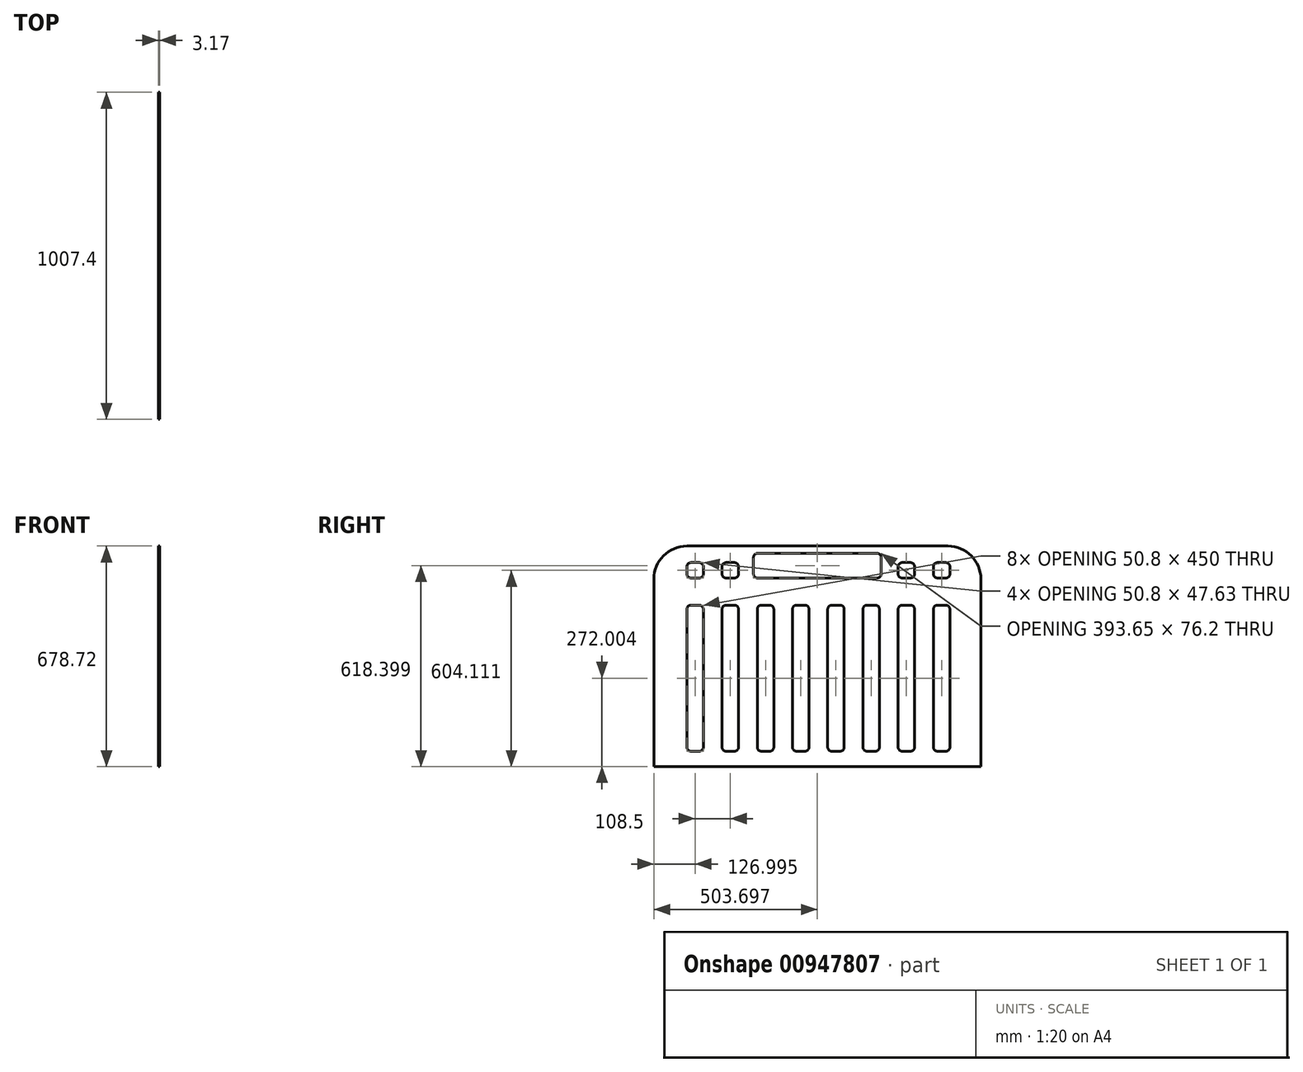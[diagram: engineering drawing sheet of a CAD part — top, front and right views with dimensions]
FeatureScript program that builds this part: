
annotation { "Feature Type Name" : "Feature", "Feature Type Description" : "" }
export const myFeature = defineFeature(function(context is Context, id is Id, definition is map)
    precondition{}
    {
        {
            var Q0;
            Q0=qCreatedBy(makeId("Right.planeOp"),FACE);
            var sketch = newSketch(context, id + "F0", { "sketchPlane" : qUnion([Q0])});
            skLineSegment(sketch, "E0", {"start": v(-521.4, 162.17) * mm, "end": v(-521.4, -414.95) * mm});
            skLineSegment(sketch, "E1", {"start": v(-521.4, -414.95) * mm, "end": v(486, -414.95) * mm});
            skLineSegment(sketch, "E2", {"start": v(486, -414.95) * mm, "end": v(486, 162.17) * mm});
            skLineSegment(sketch, "E3", {"start": v(-419.8, 263.77) * mm, "end": v(384.4, 263.77) * mm});
            skArc(sketch, "E4", {"start": v(486, 162.17) * mm, "mid": v(456.24, 234.02) * mm, "end": v(384.4, 263.77) * mm});
            skArc(sketch, "E5", {"start": v(-419.8, 263.77) * mm, "mid": v(-491.65, 234.02) * mm, "end": v(-521.4, 162.17) * mm});
            skLineSegment(sketch, "E6.bottom", {"start": v(-407.1, 82.05) * mm, "end": v(-381.7, 82.05) * mm});
            skLineSegment(sketch, "E6.top", {"start": v(-407.1, -367.95) * mm, "end": v(-381.7, -367.95) * mm});
            skLineSegment(sketch, "E6.left", {"start": v(-419.8, 69.35) * mm, "end": v(-419.8, -355.25) * mm});
            skLineSegment(sketch, "E6.right", {"start": v(-369, 69.35) * mm, "end": v(-369, -355.25) * mm});
            skPoint(sketch, "E7.visualSharp", {"position": v(-419.8, 82.05) * mm});
            skArc(sketch, "E7.filletArc", {"start": v(-407.1, 82.05) * mm, "mid": v(-416.08, 78.33) * mm, "end": v(-419.8, 69.35) * mm});
            skPoint(sketch, "E8.visualSharp", {"position": v(-369, 82.05) * mm});
            skArc(sketch, "E8.filletArc", {"start": v(-369, 69.35) * mm, "mid": v(-372.72, 78.33) * mm, "end": v(-381.7, 82.05) * mm});
            skPoint(sketch, "E9.visualSharp", {"position": v(-369, -367.95) * mm});
            skArc(sketch, "E9.filletArc", {"start": v(-381.7, -367.95) * mm, "mid": v(-372.72, -364.23) * mm, "end": v(-369, -355.25) * mm});
            skPoint(sketch, "E10.visualSharp", {"position": v(-419.8, -367.95) * mm});
            skArc(sketch, "E10.filletArc", {"start": v(-419.8, -355.25) * mm, "mid": v(-416.08, -364.23) * mm, "end": v(-407.1, -367.95) * mm});
            skPoint(sketch, "E11.1.0.0", {"position": v(-311.3, -367.95) * mm});
            skPoint(sketch, "E11.1.0.1", {"position": v(-260.5, -367.95) * mm});
            skPoint(sketch, "E11.1.0.2", {"position": v(-311.3, 114.55) * mm});
            skLineSegment(sketch, "E11.1.0.3", {"start": v(-311.3, 69.35) * mm, "end": v(-311.3, -355.25) * mm});
            skPoint(sketch, "E11.1.0.4", {"position": v(-260.5, 82.05) * mm});
            skLineSegment(sketch, "E11.1.0.5", {"start": v(-260.5, 69.35) * mm, "end": v(-260.5, -355.25) * mm});
            skArc(sketch, "E11.1.0.6", {"start": v(-260.5, 69.35) * mm, "mid": v(-264.22, 78.33) * mm, "end": v(-273.2, 82.05) * mm});
            skLineSegment(sketch, "E11.1.0.7", {"start": v(-298.6, -367.95) * mm, "end": v(-273.2, -367.95) * mm});
            skLineSegment(sketch, "E11.1.0.8", {"start": v(-298.6, 82.05) * mm, "end": v(-273.2, 82.05) * mm});
            skArc(sketch, "E11.1.0.9", {"start": v(-311.3, -355.25) * mm, "mid": v(-307.58, -364.23) * mm, "end": v(-298.6, -367.95) * mm});
            skArc(sketch, "E11.1.0.10", {"start": v(-298.6, 82.05) * mm, "mid": v(-307.58, 78.33) * mm, "end": v(-311.3, 69.35) * mm});
            skArc(sketch, "E11.1.0.11", {"start": v(-273.2, -367.95) * mm, "mid": v(-264.22, -364.23) * mm, "end": v(-260.5, -355.25) * mm});
            skPoint(sketch, "E11.2.0.0", {"position": v(-202.8, -367.95) * mm});
            skPoint(sketch, "E11.2.0.1", {"position": v(-152, -367.95) * mm});
            skPoint(sketch, "E11.2.0.2", {"position": v(-202.8, 114.55) * mm});
            skLineSegment(sketch, "E11.2.0.3", {"start": v(-202.8, 69.35) * mm, "end": v(-202.8, -355.25) * mm});
            skPoint(sketch, "E11.2.0.4", {"position": v(-152, 114.55) * mm});
            skLineSegment(sketch, "E11.2.0.5", {"start": v(-152, 69.35) * mm, "end": v(-152, -355.25) * mm});
            skArc(sketch, "E11.2.0.6", {"start": v(-152, 69.35) * mm, "mid": v(-155.72, 78.33) * mm, "end": v(-164.7, 82.05) * mm});
            skLineSegment(sketch, "E11.2.0.7", {"start": v(-190.1, -367.95) * mm, "end": v(-164.7, -367.95) * mm});
            skLineSegment(sketch, "E11.2.0.8", {"start": v(-190.1, 82.05) * mm, "end": v(-164.7, 82.05) * mm});
            skArc(sketch, "E11.2.0.9", {"start": v(-202.8, -355.25) * mm, "mid": v(-199.08, -364.23) * mm, "end": v(-190.1, -367.95) * mm});
            skArc(sketch, "E11.2.0.10", {"start": v(-190.1, 82.05) * mm, "mid": v(-199.08, 78.33) * mm, "end": v(-202.8, 69.35) * mm});
            skArc(sketch, "E11.2.0.11", {"start": v(-164.7, -367.95) * mm, "mid": v(-155.72, -364.23) * mm, "end": v(-152, -355.25) * mm});
            skPoint(sketch, "E11.3.0.0", {"position": v(-94.3, -367.95) * mm});
            skPoint(sketch, "E11.3.0.1", {"position": v(-43.5, -367.95) * mm});
            skPoint(sketch, "E11.3.0.2", {"position": v(-94.3, 114.55) * mm});
            skLineSegment(sketch, "E11.3.0.3", {"start": v(-94.3, 69.35) * mm, "end": v(-94.3, -355.25) * mm});
            skPoint(sketch, "E11.3.0.4", {"position": v(-43.5, 114.55) * mm});
            skLineSegment(sketch, "E11.3.0.5", {"start": v(-43.5, 69.35) * mm, "end": v(-43.5, -355.25) * mm});
            skArc(sketch, "E11.3.0.6", {"start": v(-43.5, 69.35) * mm, "mid": v(-47.22, 78.33) * mm, "end": v(-56.2, 82.05) * mm});
            skLineSegment(sketch, "E11.3.0.7", {"start": v(-81.6, -367.95) * mm, "end": v(-56.2, -367.95) * mm});
            skLineSegment(sketch, "E11.3.0.8", {"start": v(-81.6, 82.05) * mm, "end": v(-56.2, 82.05) * mm});
            skArc(sketch, "E11.3.0.9", {"start": v(-94.3, -355.25) * mm, "mid": v(-90.58, -364.23) * mm, "end": v(-81.6, -367.95) * mm});
            skArc(sketch, "E11.3.0.10", {"start": v(-81.6, 82.05) * mm, "mid": v(-90.58, 78.33) * mm, "end": v(-94.3, 69.35) * mm});
            skArc(sketch, "E11.3.0.11", {"start": v(-56.2, -367.95) * mm, "mid": v(-47.22, -364.23) * mm, "end": v(-43.5, -355.25) * mm});
            skPoint(sketch, "E11.4.0.0", {"position": v(14.2, -367.95) * mm});
            skPoint(sketch, "E11.4.0.1", {"position": v(65, -367.95) * mm});
            skPoint(sketch, "E11.4.0.2", {"position": v(14.2, 114.55) * mm});
            skLineSegment(sketch, "E11.4.0.3", {"start": v(14.2, 69.35) * mm, "end": v(14.2, -355.25) * mm});
            skPoint(sketch, "E11.4.0.4", {"position": v(65, 114.55) * mm});
            skLineSegment(sketch, "E11.4.0.5", {"start": v(65, 69.35) * mm, "end": v(65, -355.25) * mm});
            skArc(sketch, "E11.4.0.6", {"start": v(65, 69.35) * mm, "mid": v(61.28, 78.33) * mm, "end": v(52.3, 82.05) * mm});
            skLineSegment(sketch, "E11.4.0.7", {"start": v(26.9, -367.95) * mm, "end": v(52.3, -367.95) * mm});
            skLineSegment(sketch, "E11.4.0.8", {"start": v(26.9, 82.05) * mm, "end": v(52.3, 82.05) * mm});
            skArc(sketch, "E11.4.0.9", {"start": v(14.2, -355.25) * mm, "mid": v(17.92, -364.23) * mm, "end": v(26.9, -367.95) * mm});
            skArc(sketch, "E11.4.0.10", {"start": v(26.9, 82.05) * mm, "mid": v(17.92, 78.33) * mm, "end": v(14.2, 69.35) * mm});
            skArc(sketch, "E11.4.0.11", {"start": v(52.3, -367.95) * mm, "mid": v(61.28, -364.23) * mm, "end": v(65, -355.25) * mm});
            skPoint(sketch, "E11.5.0.0", {"position": v(122.7, -367.95) * mm});
            skPoint(sketch, "E11.5.0.1", {"position": v(173.5, -367.95) * mm});
            skPoint(sketch, "E11.5.0.2", {"position": v(122.7, 114.55) * mm});
            skLineSegment(sketch, "E11.5.0.3", {"start": v(122.7, 69.35) * mm, "end": v(122.7, -355.25) * mm});
            skPoint(sketch, "E11.5.0.4", {"position": v(173.5, 114.55) * mm});
            skLineSegment(sketch, "E11.5.0.5", {"start": v(173.5, 69.35) * mm, "end": v(173.5, -355.25) * mm});
            skArc(sketch, "E11.5.0.6", {"start": v(173.5, 69.35) * mm, "mid": v(169.78, 78.33) * mm, "end": v(160.8, 82.05) * mm});
            skLineSegment(sketch, "E11.5.0.7", {"start": v(135.4, -367.95) * mm, "end": v(160.8, -367.95) * mm});
            skLineSegment(sketch, "E11.5.0.8", {"start": v(135.4, 82.05) * mm, "end": v(160.8, 82.05) * mm});
            skArc(sketch, "E11.5.0.9", {"start": v(122.7, -355.25) * mm, "mid": v(126.42, -364.23) * mm, "end": v(135.4, -367.95) * mm});
            skArc(sketch, "E11.5.0.10", {"start": v(135.4, 82.05) * mm, "mid": v(126.42, 78.33) * mm, "end": v(122.7, 69.35) * mm});
            skArc(sketch, "E11.5.0.11", {"start": v(160.8, -367.95) * mm, "mid": v(169.78, -364.23) * mm, "end": v(173.5, -355.25) * mm});
            skPoint(sketch, "E11.6.0.0", {"position": v(231.2, -367.95) * mm});
            skPoint(sketch, "E11.6.0.1", {"position": v(282, -367.95) * mm});
            skPoint(sketch, "E11.6.0.2", {"position": v(231.2, 114.55) * mm});
            skLineSegment(sketch, "E11.6.0.3", {"start": v(231.2, 69.35) * mm, "end": v(231.2, -355.25) * mm});
            skPoint(sketch, "E11.6.0.4", {"position": v(282, 114.55) * mm});
            skLineSegment(sketch, "E11.6.0.5", {"start": v(282, 69.35) * mm, "end": v(282, -355.25) * mm});
            skArc(sketch, "E11.6.0.6", {"start": v(282, 69.35) * mm, "mid": v(278.28, 78.33) * mm, "end": v(269.3, 82.05) * mm});
            skLineSegment(sketch, "E11.6.0.7", {"start": v(243.9, -367.95) * mm, "end": v(269.3, -367.95) * mm});
            skLineSegment(sketch, "E11.6.0.8", {"start": v(243.9, 82.05) * mm, "end": v(269.3, 82.05) * mm});
            skArc(sketch, "E11.6.0.9", {"start": v(231.2, -355.25) * mm, "mid": v(234.92, -364.23) * mm, "end": v(243.9, -367.95) * mm});
            skArc(sketch, "E11.6.0.10", {"start": v(243.9, 82.05) * mm, "mid": v(234.92, 78.33) * mm, "end": v(231.2, 69.35) * mm});
            skArc(sketch, "E11.6.0.11", {"start": v(269.3, -367.95) * mm, "mid": v(278.28, -364.23) * mm, "end": v(282, -355.25) * mm});
            skPoint(sketch, "E11.7.0.0", {"position": v(339.7, -367.95) * mm});
            skPoint(sketch, "E11.7.0.1", {"position": v(390.5, -367.95) * mm});
            skPoint(sketch, "E11.7.0.2", {"position": v(339.7, 114.55) * mm});
            skLineSegment(sketch, "E11.7.0.3", {"start": v(339.7, 69.35) * mm, "end": v(339.7, -355.25) * mm});
            skPoint(sketch, "E11.7.0.4", {"position": v(390.5, 114.55) * mm});
            skLineSegment(sketch, "E11.7.0.5", {"start": v(390.5, 69.35) * mm, "end": v(390.5, -355.25) * mm});
            skArc(sketch, "E11.7.0.6", {"start": v(390.5, 69.35) * mm, "mid": v(386.78, 78.33) * mm, "end": v(377.8, 82.05) * mm});
            skLineSegment(sketch, "E11.7.0.7", {"start": v(352.4, -367.95) * mm, "end": v(377.8, -367.95) * mm});
            skLineSegment(sketch, "E11.7.0.8", {"start": v(352.4, 82.05) * mm, "end": v(377.8, 82.05) * mm});
            skArc(sketch, "E11.7.0.9", {"start": v(339.7, -355.25) * mm, "mid": v(343.42, -364.23) * mm, "end": v(352.4, -367.95) * mm});
            skArc(sketch, "E11.7.0.10", {"start": v(352.4, 82.05) * mm, "mid": v(343.42, 78.33) * mm, "end": v(339.7, 69.35) * mm});
            skArc(sketch, "E11.7.0.11", {"start": v(377.8, -367.95) * mm, "mid": v(386.78, -364.23) * mm, "end": v(390.5, -355.25) * mm});
            skPoint(sketch, "E12.visualSharp", {"position": v(-470.6, 212.97) * mm});
            skPoint(sketch, "E13.visualSharp", {"position": v(435.2, 212.97) * mm});
            skPoint(sketch, "E14.visualSharp", {"position": v(435.2, 165.35) * mm});
            skPoint(sketch, "E15.visualSharp", {"position": v(-470.6, 165.35) * mm});
            skLineSegment(sketch, "E16", {"start": v(-311.3, 178.05) * mm, "end": v(-311.3, 200.27) * mm});
            skLineSegment(sketch, "E17", {"start": v(-260.5, 178.05) * mm, "end": v(-260.5, 200.27) * mm});
            skLineSegment(sketch, "E18", {"start": v(-407.1, 212.97) * mm, "end": v(-381.7, 212.97) * mm});
            skLineSegment(sketch, "E19", {"start": v(-407.1, 165.35) * mm, "end": v(-381.7, 165.35) * mm});
            skLineSegment(sketch, "E20", {"start": v(-419.8, 178.05) * mm, "end": v(-419.8, 200.27) * mm});
            skLineSegment(sketch, "E21", {"start": v(-369, 178.05) * mm, "end": v(-369, 200.27) * mm});
            skLineSegment(sketch, "E22", {"start": v(231.2, 178.05) * mm, "end": v(231.2, 200.27) * mm});
            skLineSegment(sketch, "E23", {"start": v(282, 178.05) * mm, "end": v(282, 200.27) * mm});
            skLineSegment(sketch, "E24", {"start": v(339.7, 178.05) * mm, "end": v(339.7, 200.27) * mm});
            skLineSegment(sketch, "E25", {"start": v(390.5, 178.05) * mm, "end": v(390.5, 200.27) * mm});
            skLineSegment(sketch, "E26.trimOffspring", {"start": v(-298.6, 212.97) * mm, "end": v(-273.2, 212.97) * mm});
            skLineSegment(sketch, "E27.trimOffspring", {"start": v(-298.6, 165.35) * mm, "end": v(-273.2, 165.35) * mm});
            skLineSegment(sketch, "E28.trimOffspring", {"start": v(243.9, 212.97) * mm, "end": v(269.3, 212.97) * mm});
            skLineSegment(sketch, "E29.trimOffspring", {"start": v(243.9, 165.35) * mm, "end": v(269.3, 165.35) * mm});
            skLineSegment(sketch, "E30.trimOffspring", {"start": v(352.4, 165.35) * mm, "end": v(377.8, 165.35) * mm});
            skLineSegment(sketch, "E31.trimOffspring", {"start": v(352.4, 212.97) * mm, "end": v(377.8, 212.97) * mm});
            skPoint(sketch, "E32.visualSharp", {"position": v(-419.8, 212.97) * mm});
            skArc(sketch, "E32.filletArc", {"start": v(-407.1, 212.97) * mm, "mid": v(-416.08, 209.25) * mm, "end": v(-419.8, 200.27) * mm});
            skPoint(sketch, "E33.visualSharp", {"position": v(-369, 165.35) * mm});
            skArc(sketch, "E33.filletArc", {"start": v(-381.7, 165.35) * mm, "mid": v(-372.72, 169.07) * mm, "end": v(-369, 178.05) * mm});
            skPoint(sketch, "E34.visualSharp", {"position": v(-369, 212.97) * mm});
            skArc(sketch, "E34.filletArc", {"start": v(-369, 200.27) * mm, "mid": v(-372.72, 209.25) * mm, "end": v(-381.7, 212.97) * mm});
            skPoint(sketch, "E35.visualSharp", {"position": v(-419.8, 165.35) * mm});
            skArc(sketch, "E35.filletArc", {"start": v(-419.8, 178.05) * mm, "mid": v(-416.08, 169.07) * mm, "end": v(-407.1, 165.35) * mm});
            skPoint(sketch, "E36.visualSharp", {"position": v(-311.3, 212.97) * mm});
            skArc(sketch, "E36.filletArc", {"start": v(-298.6, 212.97) * mm, "mid": v(-307.58, 209.25) * mm, "end": v(-311.3, 200.27) * mm});
            skPoint(sketch, "E37.visualSharp", {"position": v(-260.5, 165.35) * mm});
            skArc(sketch, "E37.filletArc", {"start": v(-273.2, 165.35) * mm, "mid": v(-264.22, 169.07) * mm, "end": v(-260.5, 178.05) * mm});
            skPoint(sketch, "E38.visualSharp", {"position": v(-260.5, 212.97) * mm});
            skArc(sketch, "E38.filletArc", {"start": v(-260.5, 200.27) * mm, "mid": v(-264.22, 209.25) * mm, "end": v(-273.2, 212.97) * mm});
            skPoint(sketch, "E39.visualSharp", {"position": v(-311.3, 165.35) * mm});
            skArc(sketch, "E39.filletArc", {"start": v(-311.3, 178.05) * mm, "mid": v(-307.58, 169.07) * mm, "end": v(-298.6, 165.35) * mm});
            skPoint(sketch, "E40.visualSharp", {"position": v(231.2, 212.97) * mm});
            skArc(sketch, "E40.filletArc", {"start": v(243.9, 212.97) * mm, "mid": v(234.92, 209.25) * mm, "end": v(231.2, 200.27) * mm});
            skPoint(sketch, "E41.visualSharp", {"position": v(282, 212.97) * mm});
            skArc(sketch, "E41.filletArc", {"start": v(282, 200.27) * mm, "mid": v(278.28, 209.25) * mm, "end": v(269.3, 212.97) * mm});
            skPoint(sketch, "E42.visualSharp", {"position": v(282, 165.35) * mm});
            skArc(sketch, "E42.filletArc", {"start": v(269.3, 165.35) * mm, "mid": v(278.28, 169.07) * mm, "end": v(282, 178.05) * mm});
            skPoint(sketch, "E43.visualSharp", {"position": v(231.2, 165.35) * mm});
            skArc(sketch, "E43.filletArc", {"start": v(231.2, 178.05) * mm, "mid": v(234.92, 169.07) * mm, "end": v(243.9, 165.35) * mm});
            skPoint(sketch, "E44.visualSharp", {"position": v(339.7, 212.97) * mm});
            skArc(sketch, "E44.filletArc", {"start": v(352.4, 212.97) * mm, "mid": v(343.42, 209.25) * mm, "end": v(339.7, 200.27) * mm});
            skPoint(sketch, "E45.visualSharp", {"position": v(390.5, 212.97) * mm});
            skArc(sketch, "E45.filletArc", {"start": v(390.5, 200.27) * mm, "mid": v(386.78, 209.25) * mm, "end": v(377.8, 212.97) * mm});
            skPoint(sketch, "E46.visualSharp", {"position": v(390.5, 165.35) * mm});
            skArc(sketch, "E46.filletArc", {"start": v(377.8, 165.35) * mm, "mid": v(386.78, 169.07) * mm, "end": v(390.5, 178.05) * mm});
            skPoint(sketch, "E47.visualSharp", {"position": v(339.7, 165.35) * mm});
            skArc(sketch, "E47.filletArc", {"start": v(339.7, 178.05) * mm, "mid": v(343.42, 169.07) * mm, "end": v(352.4, 165.35) * mm});
            skLineSegment(sketch, "E48.bottom", {"start": v(-201.83, 165.35) * mm, "end": v(166.42, 165.35) * mm});
            skLineSegment(sketch, "E48.top", {"start": v(-201.83, 241.55) * mm, "end": v(166.42, 241.55) * mm});
            skLineSegment(sketch, "E48.left", {"start": v(-214.53, 178.05) * mm, "end": v(-214.53, 228.85) * mm});
            skLineSegment(sketch, "E48.right", {"start": v(179.12, 178.05) * mm, "end": v(179.12, 228.85) * mm});
            skPoint(sketch, "E49", {"position": v(-17.7, 241.55) * mm});
            skPoint(sketch, "E50", {"position": v(-17.7, 263.77) * mm});
            skLineSegment(sketch, "E51", {"start": v(-17.7, 241.55) * mm, "end": v(-17.7, 290.92) * mm});
            skPoint(sketch, "E52.visualSharp", {"position": v(-214.53, 241.55) * mm});
            skArc(sketch, "E52.filletArc", {"start": v(-201.83, 241.55) * mm, "mid": v(-210.8, 237.83) * mm, "end": v(-214.53, 228.85) * mm});
            skPoint(sketch, "E53.visualSharp", {"position": v(179.12, 241.55) * mm});
            skArc(sketch, "E53.filletArc", {"start": v(179.12, 228.85) * mm, "mid": v(175.4, 237.83) * mm, "end": v(166.42, 241.55) * mm});
            skPoint(sketch, "E54.visualSharp", {"position": v(179.12, 165.35) * mm});
            skArc(sketch, "E54.filletArc", {"start": v(166.42, 165.35) * mm, "mid": v(175.4, 169.07) * mm, "end": v(179.12, 178.05) * mm});
            skPoint(sketch, "E55.visualSharp", {"position": v(-214.53, 165.35) * mm});
            skArc(sketch, "E55.filletArc", {"start": v(-214.53, 178.05) * mm, "mid": v(-210.8, 169.07) * mm, "end": v(-201.83, 165.35) * mm});
            skSolve(sketch);
        }
        {
            var Q0;
            Q0 = qSketchRegion(id + "F0", true);
            extrude(context, id + "F1", {"entities" : qUnion([Q0]), "depth" : 3.17 * mm, "offsetDistance" : 25 * mm});
        }
    });
